# Revit family: 216D
name_source: partatom
category: Lighting Fixtures
revit_build: Autodesk Revit 2014 (Build: 20130308_1515(x64)
units: mm (PartAtom-declared; Revit-internal decimal feet)

## types (1)
- 216D
    Apparent Load = 50 VA
    Assembly Code = D5020200
    Color Filter = 16777215
    Connector Description = Lighting Connector
    Default Elevation = 1219.2 mm  [stored 4 ft]
    Description = The 216 well-glass luminaire is ideal for use where a compact, robust and efficient source of localised lighting is needed. Designed for use in Zone 1 and 21 hazardous areas, the rangeaccommodates high pressure sodium lamps up to 70W. The 216 is made from corrosion resistant aluminium alloy and toughened boro-silicate glass using stainless steel fastenings and has an IP66/67 rating. The luminaire features a large side mounted increased safety terminal chamber eliminating the need for flame-proof cable glands and allowing flush mounting.
    Dimming Lamp Color Temperature Shift = <None>
    Emit Shape Visible in Rendering = No
    Emit from Circle Diameter = 50 mm  [stored 0.164042 ft]
    Features = Installation to gas groups IIA and IIB
Highly resistant to mechanical damage and corrosion.
Stainless steel fasteners.
Compact and efficient.
Ex e terminal chamber.
Anchor chain on glass cover assembly.
Suitable for use down to -50˚C ambient.
ATEX Certified and EAC Approved.
    Fixture distribution = Direct
    Glass = Hubbell - Glass
    Height = 535 mm
    Housing Material = Paint - Hubbell - White Texture
    IP Rating = IP66/67
    Inner Length = 200 mm  [stored 0.656168 ft]
    Lamp = LED
    Length = 270 mm  [stored 0.885827 ft]
    Load Classification = Lighting
    Manufacturer = Chalmit
    Model = 216D
    Mounting = Paint - Hubbell - Light Silver
    Photometric Web File = CHL_216D_050_HS.ies
    Power Factor = 1
    Product Documentation Link = https://hubbellcdn.com
    Product Link = https://www.hubbell.com
    Reflector Finish = Hubbell - White Glass
    Tilt Angle = 90.00°
    URL = https://www.hubbell.com
    Voltage = 120 V
    Warranty = 5 years Warranty
    Wattage Comments = 50W
    Watts = 50 W
    Width = 280 mm  [stored 0.918635 ft]
    Wings = Paint - Hubbell - Light Silver

note: [stored X ft] marks values corroborated as IEEE doubles in the binary element streams (Revit-internal decimal feet)

## geometry (parser evidence)
native form markers: Sweep x4
no freeform markers — native parametric forms only
